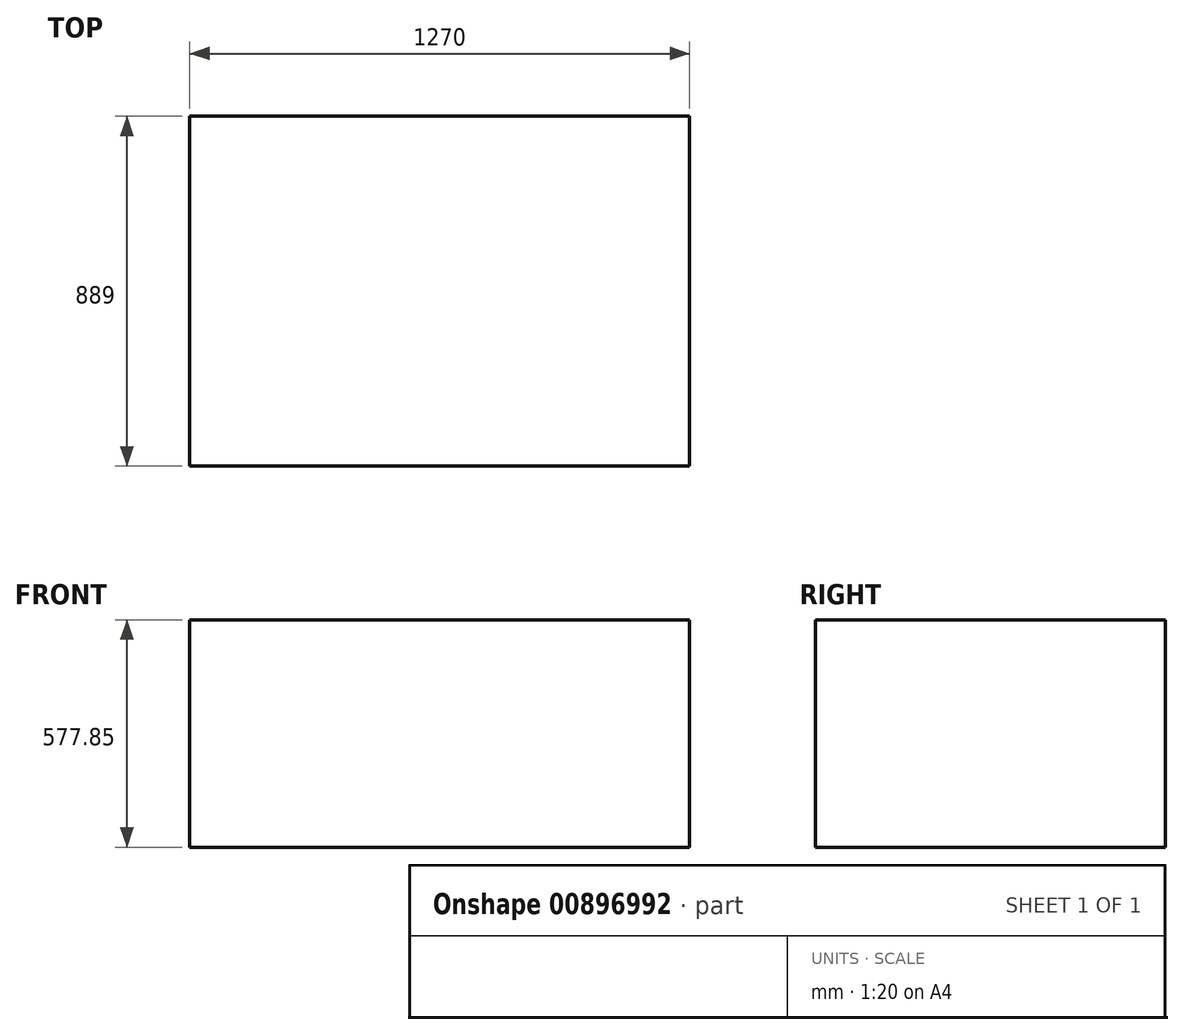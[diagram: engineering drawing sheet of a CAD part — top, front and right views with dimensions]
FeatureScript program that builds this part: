
annotation { "Feature Type Name" : "Feature", "Feature Type Description" : "" }
export const myFeature = defineFeature(function(context is Context, id is Id, definition is map)
    precondition{}
    {
        {
            var Q0;
            Q0=qCreatedBy(makeId("Top.planeOp"),FACE);
            var sketch = newSketch(context, id + "F0", { "sketchPlane" : qUnion([Q0])});
            skLineSegment(sketch, "E0.bottom", {"start": v(0, 0) * mm, "end": v(1270, 0) * mm});
            skLineSegment(sketch, "E0.top", {"start": v(0, 889) * mm, "end": v(1270, 889) * mm});
            skLineSegment(sketch, "E0.left", {"start": v(0, 0) * mm, "end": v(0, 889) * mm});
            skLineSegment(sketch, "E0.right", {"start": v(1270, 0) * mm, "end": v(1270, 889) * mm});
            skSolve(sketch);
        }
        {
            var Q0;
            Q0 = qSketchRegion(id + "F0", true);
            extrude(context, id + "F1", {"entities" : qUnion([Q0]), "depth" : 577.85 * mm, "offsetDistance" : 25.4 * mm});
        }
    });
